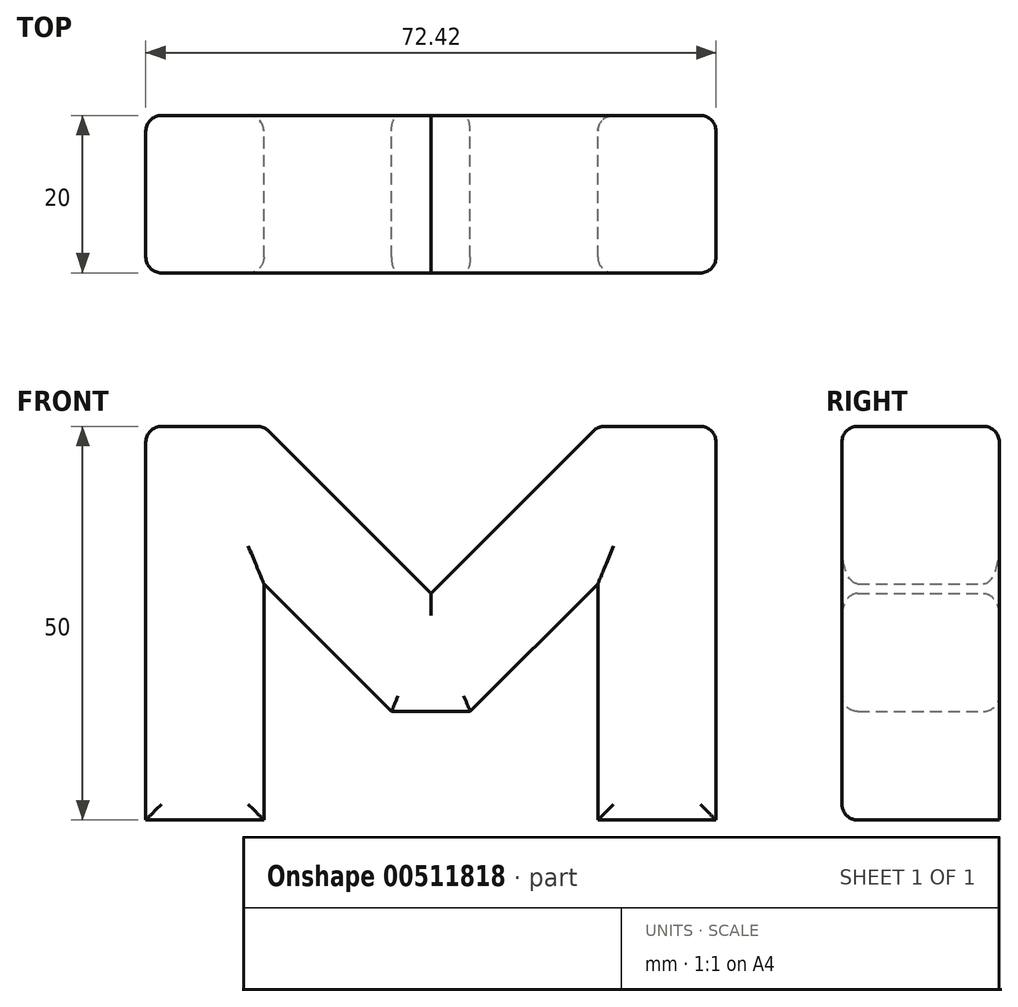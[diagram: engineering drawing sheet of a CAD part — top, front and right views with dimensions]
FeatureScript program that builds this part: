
annotation { "Feature Type Name" : "Feature", "Feature Type Description" : "" }
export const myFeature = defineFeature(function(context is Context, id is Id, definition is map)
    precondition{}
    {
        {
            var Q0;
            Q0=qCreatedBy(makeId("Front.planeOp"),FACE);
            var sketch = newSketch(context, id + "F0", { "sketchPlane" : qUnion([Q0])});
            skLineSegment(sketch, "E0", {"start": v(0, 0) * mm, "end": v(-21.21, 21.21) * mm});
            skLineSegment(sketch, "E1", {"start": v(-21.21, 21.21) * mm, "end": v(-36.21, 21.21) * mm});
            skLineSegment(sketch, "E2", {"start": v(-36.21, 21.21) * mm, "end": v(-36.21, -28.79) * mm});
            skLineSegment(sketch, "E3", {"start": v(-36.21, -28.79) * mm, "end": v(-21.21, -28.79) * mm});
            skLineSegment(sketch, "E4", {"start": v(-21.21, -28.79) * mm, "end": v(-21.21, 1.21) * mm});
            skLineSegment(sketch, "E5", {"start": v(0, 0) * mm, "end": v(21.21, 21.21) * mm});
            skPoint(sketch, "E6.end.orphan", {"position": v(12.77, 0) * mm});
            skLineSegment(sketch, "E7", {"start": v(21.21, 21.21) * mm, "end": v(36.21, 21.21) * mm});
            skLineSegment(sketch, "E8", {"start": v(36.21, 21.21) * mm, "end": v(36.21, -28.79) * mm});
            skLineSegment(sketch, "E9", {"start": v(36.21, -28.79) * mm, "end": v(21.21, -28.79) * mm});
            skLineSegment(sketch, "E10", {"start": v(21.21, -28.79) * mm, "end": v(21.21, 1.21) * mm});
            skLineSegment(sketch, "E11", {"start": v(-21.21, 1.21) * mm, "end": v(-5, -15) * mm});
            skLineSegment(sketch, "E12", {"start": v(-5, -15) * mm, "end": v(5, -15) * mm});
            skLineSegment(sketch, "E13", {"start": v(5, -15) * mm, "end": v(21.21, 1.21) * mm});
            skSolve(sketch);
        }
        {
            var Q0;
            Q0=makeQuery(id+"F0.imprint","IMPRINT",FACE,{"disambiguationData":[TD([[makeQuery(id+"F0.imprint","IMPRINT",EDGE,{"derivedFrom":sQuery(id+"F0.wireOp",EDGE,"E0")}),1.0]])]});
            extrude(context, id + "F1", {"entities" : qUnion([Q0]), "depth" : 20 * mm});
        }
        {
            var Q0;
            Q0=makeQuery(id+"F1.opExtrude","CAP_EDGE",EDGE,{"disambiguationData":[OSD([sQuery(id+"F0.wireOp",EDGE,"E2")])],"isStart":false});
            var Q1;
            Q1=makeQuery(id+"F1.opExtrude","CAP_EDGE",EDGE,{"disambiguationData":[OSD([sQuery(id+"F0.wireOp",EDGE,"E8")])],"isStart":false});
            var Q2;
            Q2=makeQuery(id+"F1.opExtrude","CAP_EDGE",EDGE,{"disambiguationData":[OSD([sQuery(id+"F0.wireOp",EDGE,"E7")])],"isStart":false});
            var Q3;
            Q3=makeQuery(id+"F1.opExtrude","SWEPT_EDGE",EDGE,{"disambiguationData":[OSD([sQuery(id+"F0.wireOp",EDGE,"E7"),sQuery(id+"F0.wireOp",EDGE,"E8")])]});
            var Q4;
            Q4=makeQuery(id+"F1.opExtrude","CAP_EDGE",EDGE,{"disambiguationData":[OSD([sQuery(id+"F0.wireOp",EDGE,"E8")])],"isStart":true});
            var Q5;
            Q5=makeQuery(id+"F1.opExtrude","CAP_EDGE",EDGE,{"disambiguationData":[OSD([sQuery(id+"F0.wireOp",EDGE,"E7")])],"isStart":true});
            var Q6;
            Q6=makeQuery(id+"F1.opExtrude","CAP_EDGE",EDGE,{"disambiguationData":[OSD([sQuery(id+"F0.wireOp",EDGE,"E2")])],"isStart":true});
            var Q7;
            Q7=makeQuery(id+"F1.opExtrude","SWEPT_EDGE",EDGE,{"disambiguationData":[OSD([sQuery(id+"F0.wireOp",EDGE,"E1"),sQuery(id+"F0.wireOp",EDGE,"E2")])]});
            var Q8;
            Q8=makeQuery(id+"F1.opExtrude","CAP_EDGE",EDGE,{"disambiguationData":[OSD([sQuery(id+"F0.wireOp",EDGE,"E1")])],"isStart":true});
            var Q9;
            Q9=makeQuery(id+"F1.opExtrude","CAP_EDGE",EDGE,{"disambiguationData":[OSD([sQuery(id+"F0.wireOp",EDGE,"E1")])],"isStart":false});
            var Q10;
            Q10=makeQuery(id+"F1.opExtrude","CAP_EDGE",EDGE,{"disambiguationData":[OSD([sQuery(id+"F0.wireOp",EDGE,"E0")])],"isStart":true});
            var Q11;
            Q11=makeQuery(id+"F1.opExtrude","SWEPT_EDGE",EDGE,{"disambiguationData":[OSD([sQuery(id+"F0.wireOp",EDGE,"E0"),sQuery(id+"F0.wireOp",EDGE,"E1")])]});
            var Q12;
            Q12=makeQuery(id+"F1.opExtrude","CAP_EDGE",EDGE,{"disambiguationData":[OSD([sQuery(id+"F0.wireOp",EDGE,"E0")])],"isStart":false});
            var Q13;
            Q13=makeQuery(id+"F1.opExtrude","CAP_EDGE",EDGE,{"disambiguationData":[OSD([sQuery(id+"F0.wireOp",EDGE,"E5")])],"isStart":false});
            var Q14;
            Q14=makeQuery(id+"F1.opExtrude","CAP_EDGE",EDGE,{"disambiguationData":[OSD([sQuery(id+"F0.wireOp",EDGE,"E5")])],"isStart":true});
            var Q15;
            Q15=makeQuery(id+"F1.opExtrude","SWEPT_EDGE",EDGE,{"disambiguationData":[OSD([sQuery(id+"F0.wireOp",EDGE,"E5"),sQuery(id+"F0.wireOp",EDGE,"E7")])]});
            var Q16;
            Q16=makeQuery(id+"F1.opExtrude","CAP_EDGE",EDGE,{"disambiguationData":[OSD([sQuery(id+"F0.wireOp",EDGE,"E4")])],"isStart":false});
            var Q17;
            Q17=makeQuery(id+"F1.opExtrude","CAP_EDGE",EDGE,{"disambiguationData":[OSD([sQuery(id+"F0.wireOp",EDGE,"E4")])],"isStart":true});
            var Q18;
            Q18=makeQuery(id+"F1.opExtrude","CAP_EDGE",EDGE,{"disambiguationData":[OSD([sQuery(id+"F0.wireOp",EDGE,"E11")])],"isStart":false});
            var Q19;
            Q19=makeQuery(id+"F1.opExtrude","CAP_EDGE",EDGE,{"disambiguationData":[OSD([sQuery(id+"F0.wireOp",EDGE,"E13")])],"isStart":false});
            var Q20;
            Q20=makeQuery(id+"F1.opExtrude","CAP_EDGE",EDGE,{"disambiguationData":[OSD([sQuery(id+"F0.wireOp",EDGE,"E10")])],"isStart":false});
            var Q21;
            Q21=makeQuery(id+"F1.opExtrude","CAP_EDGE",EDGE,{"disambiguationData":[OSD([sQuery(id+"F0.wireOp",EDGE,"E13")])],"isStart":true});
            var Q22;
            Q22=makeQuery(id+"F1.opExtrude","CAP_EDGE",EDGE,{"disambiguationData":[OSD([sQuery(id+"F0.wireOp",EDGE,"E10")])],"isStart":true});
            var Q23;
            Q23=makeQuery(id+"F1.opExtrude","CAP_EDGE",EDGE,{"disambiguationData":[OSD([sQuery(id+"F0.wireOp",EDGE,"E11")])],"isStart":true});
            var Q24;
            Q24=makeQuery(id+"F1.opExtrude","CAP_EDGE",EDGE,{"disambiguationData":[OSD([sQuery(id+"F0.wireOp",EDGE,"E12")])],"isStart":true});
            var Q25;
            Q25=makeQuery(id+"F1.opExtrude","CAP_EDGE",EDGE,{"disambiguationData":[OSD([sQuery(id+"F0.wireOp",EDGE,"E12")])],"isStart":false});
            var Q26;
            Q26=makeQuery(id+"F1.opExtrude","CAP_FACE",FACE,{"disambiguationData":[OSD([sQuery(id+"F0.wireOp",EDGE,"E0"),sQuery(id+"F0.wireOp",EDGE,"E1"),sQuery(id+"F0.wireOp",EDGE,"E2"),sQuery(id+"F0.wireOp",EDGE,"E3"),sQuery(id+"F0.wireOp",EDGE,"E4"),sQuery(id+"F0.wireOp",EDGE,"E5"),sQuery(id+"F0.wireOp",EDGE,"E7"),sQuery(id+"F0.wireOp",EDGE,"E8"),sQuery(id+"F0.wireOp",EDGE,"E9"),sQuery(id+"F0.wireOp",EDGE,"E10"),sQuery(id+"F0.wireOp",EDGE,"E11"),sQuery(id+"F0.wireOp",EDGE,"E12"),sQuery(id+"F0.wireOp",EDGE,"E13")])],"isStart":false});
            fillet(context, id + "F2", {"entities" : qUnion([Q0, Q1, Q2, Q3, Q4, Q5, Q6, Q7, Q8, Q9, Q10, Q11, Q12, Q13, Q14, Q15, Q16, Q17, Q18, Q19, Q20, Q21, Q22, Q23, Q24, Q25, Q26]), "radius" : 2 * mm, "tangentPropagation" : true, "allowEdgeOverflow" : false});
        }
    });
